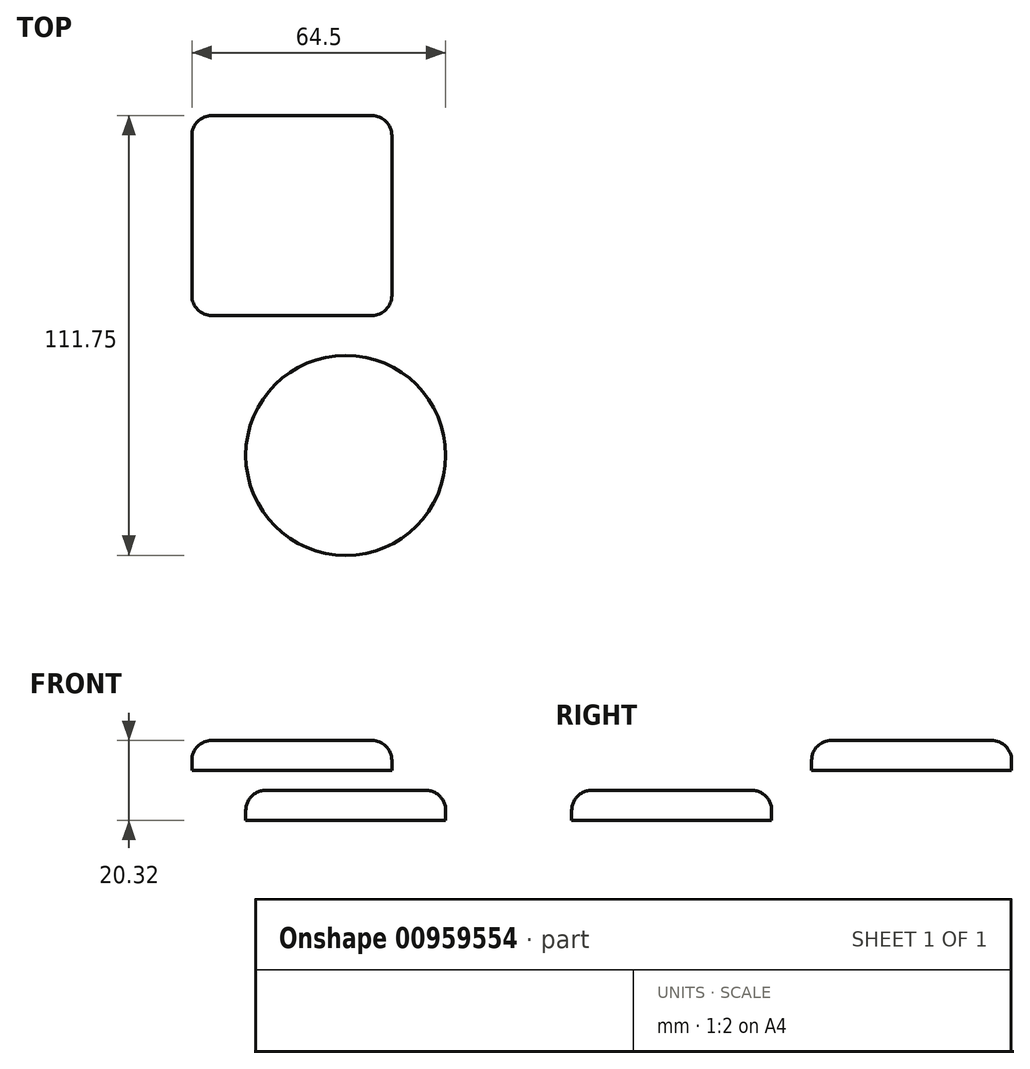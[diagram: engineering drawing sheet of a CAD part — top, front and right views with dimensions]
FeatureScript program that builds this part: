
annotation { "Feature Type Name" : "Feature", "Feature Type Description" : "" }
export const myFeature = defineFeature(function(context is Context, id is Id, definition is map)
    precondition{}
    {
        {
            var Q0;
            Q0=qCreatedBy(makeId("Top.planeOp"),FACE);
            cPlane(context, id + "F0", {"entities" : qUnion([Q0]), "cplaneType" : CPlaneType.OFFSET, "offset" : 12.7 * mm, "width" : 152.4 * mm, "height" : 152.4 * mm});
        }
        {
            var Q0;
            Q0=qCreatedBy(makeId("Top.planeOp"),FACE);
            var sketch = newSketch(context, id + "F1", { "sketchPlane" : qUnion([Q0])});
            skCircle(sketch, "E0", {"center": v(-105.31, -26.26) * mm, "radius": 25.4 * mm});
            skSolve(sketch);
        }
        {
            var Q0;
            Q0=makeQuery(id+"F1.imprint","IMPRINT",FACE,{"disambiguationData":[TD([[makeQuery(id+"F1.imprint","IMPRINT",EDGE,{"derivedFrom":sQuery(id+"F1.wireOp",EDGE,"E0")}),1.0]])]});
            extrude(context, id + "F2", {"entities" : qUnion([Q0]), "depth" : 7.62 * mm, "offsetDistance" : 25.4 * mm});
        }
        {
            var Q0;
            Q0=makeQuery(id+"F2.opExtrude","CAP_EDGE",EDGE,{"disambiguationData":[OSD([sQuery(id+"F1.wireOp",EDGE,"E0")])],"isStart":false});
            fillet(context, id + "F3", {"entities" : qUnion([Q0]), "radius" : 5.08 * mm, "tangentPropagation" : true, "allowEdgeOverflow" : false});
        }
        {
            var Q0;
            Q0=qCreatedBy(id+"F0.planeOp",FACE);
            var sketch = newSketch(context, id + "F4", { "sketchPlane" : qUnion([Q0])});
            skLineSegment(sketch, "E1.bottom", {"start": v(-93.6, 60.09) * mm, "end": v(-144.4, 60.09) * mm});
            skLineSegment(sketch, "E1.top", {"start": v(-93.6, 9.29) * mm, "end": v(-144.4, 9.29) * mm});
            skLineSegment(sketch, "E1.left", {"start": v(-93.6, 60.09) * mm, "end": v(-93.6, 9.29) * mm});
            skLineSegment(sketch, "E1.right", {"start": v(-144.4, 60.09) * mm, "end": v(-144.4, 9.29) * mm});
            skPoint(sketch, "E1.middle", {"position": v(-119, 34.69) * mm});
            skSolve(sketch);
        }
        {
            var Q0;
            Q0=makeQuery(id+"F4.imprint","IMPRINT",FACE,{"disambiguationData":[TD([[makeQuery(id+"F4.imprint","IMPRINT",EDGE,{"derivedFrom":sQuery(id+"F4.wireOp",EDGE,"E1.bottom")}),1.0]])]});
            extrude(context, id + "F5", {"entities" : qUnion([Q0]), "depth" : 7.62 * mm, "offsetDistance" : 25.4 * mm});
        }
        {
            var Q0;
            Q0=makeQuery(id+"F5.opExtrude","SWEPT_EDGE",EDGE,{"disambiguationData":[OSD([sQuery(id+"F4.wireOp",EDGE,"E1.bottom"),sQuery(id+"F4.wireOp",EDGE,"E1.left")])]});
            var Q1;
            Q1=makeQuery(id+"F5.opExtrude","SWEPT_EDGE",EDGE,{"disambiguationData":[OSD([sQuery(id+"F4.wireOp",EDGE,"E1.top"),sQuery(id+"F4.wireOp",EDGE,"E1.left")])]});
            var Q2;
            Q2=makeQuery(id+"F5.opExtrude","SWEPT_EDGE",EDGE,{"disambiguationData":[OSD([sQuery(id+"F4.wireOp",EDGE,"E1.bottom"),sQuery(id+"F4.wireOp",EDGE,"E1.right")])]});
            var Q3;
            Q3=makeQuery(id+"F5.opExtrude","SWEPT_EDGE",EDGE,{"disambiguationData":[OSD([sQuery(id+"F4.wireOp",EDGE,"E1.top"),sQuery(id+"F4.wireOp",EDGE,"E1.right")])]});
            fillet(context, id + "F6", {"entities" : qUnion([Q0, Q1, Q2, Q3]), "radius" : 5.08 * mm, "tangentPropagation" : true, "allowEdgeOverflow" : false});
        }
        {
            var Q0;
            Q0=makeQuery(id+"F5.opExtrude","CAP_FACE",FACE,{"disambiguationData":[OSD([sQuery(id+"F4.wireOp",EDGE,"E1.bottom"),sQuery(id+"F4.wireOp",EDGE,"E1.top"),sQuery(id+"F4.wireOp",EDGE,"E1.left"),sQuery(id+"F4.wireOp",EDGE,"E1.right")])],"isStart":false});
            fillet(context, id + "F7", {"entities" : qUnion([Q0]), "radius" : 5.08 * mm, "tangentPropagation" : true, "allowEdgeOverflow" : false});
        }
    });
